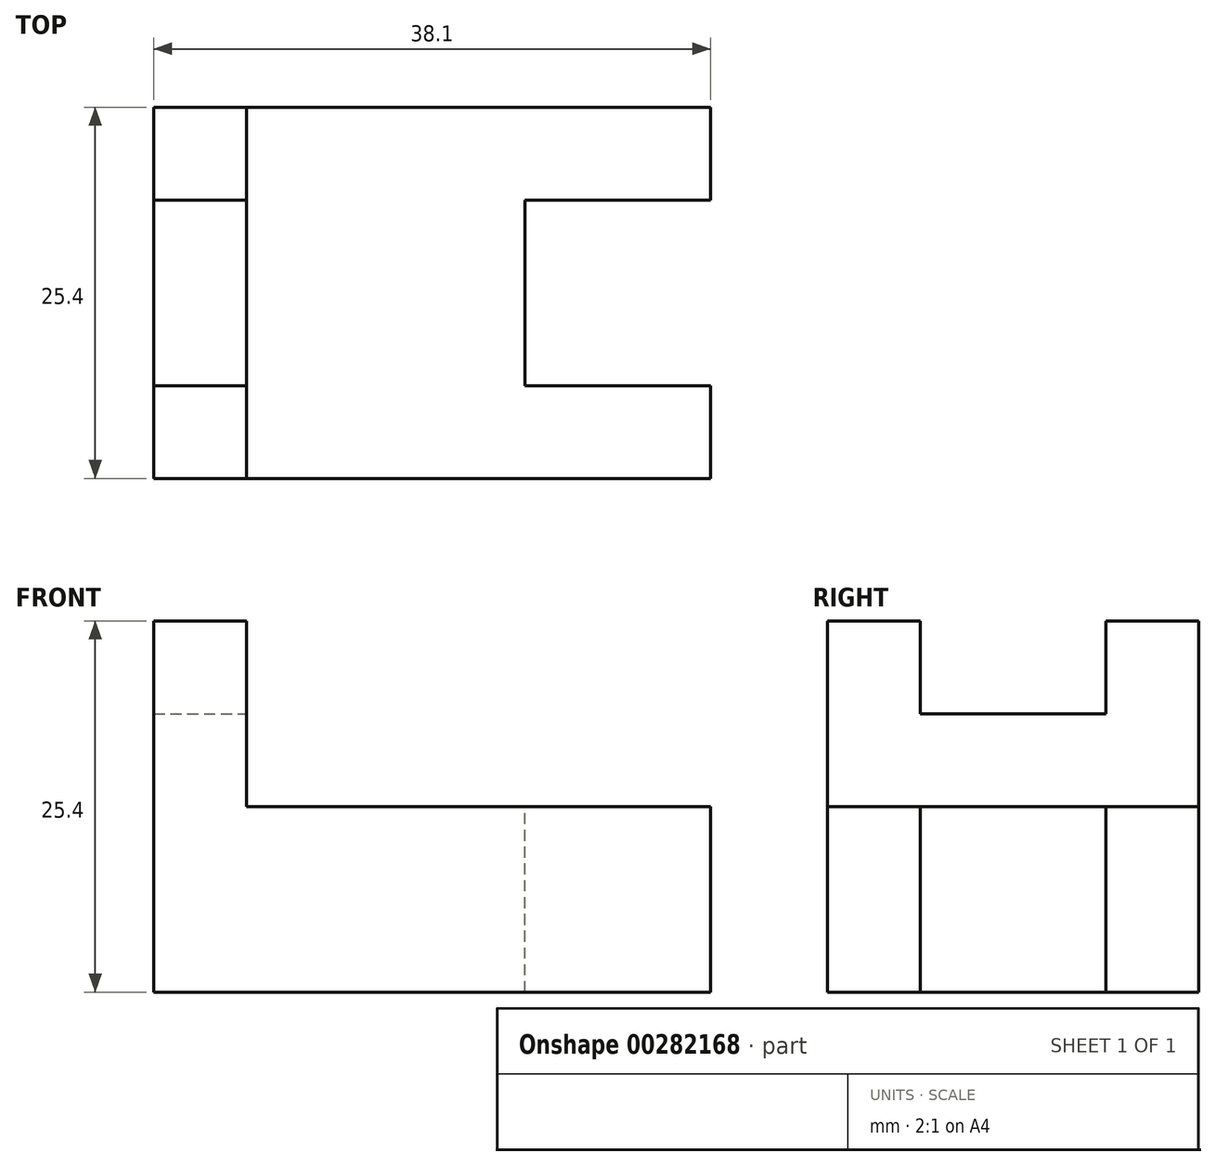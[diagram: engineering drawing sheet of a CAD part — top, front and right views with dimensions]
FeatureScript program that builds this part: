
annotation { "Feature Type Name" : "Feature", "Feature Type Description" : "" }
export const myFeature = defineFeature(function(context is Context, id is Id, definition is map)
    precondition{}
    {
        {
            var Q0;
            Q0=qCreatedBy(makeId("Front.planeOp"),FACE);
            var sketch = newSketch(context, id + "F0", { "sketchPlane" : qUnion([Q0])});
            skLineSegment(sketch, "E0", {"start": v(0, 0) * mm, "end": v(0, 25.4) * mm});
            skLineSegment(sketch, "E1", {"start": v(0, 25.4) * mm, "end": v(6.35, 25.4) * mm});
            skLineSegment(sketch, "E2", {"start": v(6.35, 25.4) * mm, "end": v(6.35, 12.7) * mm});
            skLineSegment(sketch, "E3", {"start": v(6.35, 12.7) * mm, "end": v(38.1, 12.7) * mm});
            skLineSegment(sketch, "E4", {"start": v(38.1, 12.7) * mm, "end": v(38.1, 0) * mm});
            skLineSegment(sketch, "E5", {"start": v(38.1, 0) * mm, "end": v(0, 0) * mm});
            skSolve(sketch);
        }
        {
            var Q0;
            Q0=makeQuery(id+"F0.imprint","IMPRINT",FACE,{"disambiguationData":[TD([[makeQuery(id+"F0.imprint","IMPRINT",EDGE,{"derivedFrom":sQuery(id+"F0.wireOp",EDGE,"E0")}),-1.0]])]});
            extrude(context, id + "F1", {"entities" : qUnion([Q0]), "depth" : 25.4 * mm});
        }
        {
            var Q0;
            Q0=makeQuery(id+"F1.opExtrude","SWEPT_FACE",FACE,{"disambiguationData":[OSD([sQuery(id+"F0.wireOp",EDGE,"E1")])]});
            var sketch = newSketch(context, id + "F2", { "sketchPlane" : qUnion([Q0])});
            skLineSegment(sketch, "E6.bottom", {"start": v(0, -19.05) * mm, "end": v(6.35, -19.05) * mm});
            skLineSegment(sketch, "E6.top", {"start": v(0, -6.35) * mm, "end": v(6.35, -6.35) * mm});
            skLineSegment(sketch, "E6.left", {"start": v(0, -19.05) * mm, "end": v(0, -6.35) * mm});
            skLineSegment(sketch, "E6.right", {"start": v(6.35, -19.05) * mm, "end": v(6.35, -6.35) * mm});
            skSolve(sketch);
        }
        {
            var Q0;
            Q0=makeQuery(id+"F2.imprint","IMPRINT",FACE,{"disambiguationData":[TD([[makeQuery(id+"F2.imprint","IMPRINT",EDGE,{"derivedFrom":sQuery(id+"F2.wireOp",EDGE,"E6.bottom")}),1.0]])]});
            extrude(context, id + "F3", {"entities" : qUnion([Q0]), "operationType" : NewBodyOperationType.REMOVE, "oppositeDirection" : true, "depth" : 6.35 * mm});
        }
        {
            var Q0;
            Q0=makeQuery(id+"F1.opExtrude","SWEPT_FACE",FACE,{"disambiguationData":[OSD([sQuery(id+"F0.wireOp",EDGE,"E4")])]});
            var sketch = newSketch(context, id + "F4", { "sketchPlane" : qUnion([Q0])});
            skLineSegment(sketch, "E7.bottom", {"start": v(-19.05, 0) * mm, "end": v(-6.35, 0) * mm});
            skLineSegment(sketch, "E7.top", {"start": v(-19.05, 12.7) * mm, "end": v(-6.35, 12.7) * mm});
            skLineSegment(sketch, "E7.left", {"start": v(-19.05, 0) * mm, "end": v(-19.05, 12.7) * mm});
            skLineSegment(sketch, "E7.right", {"start": v(-6.35, 0) * mm, "end": v(-6.35, 12.7) * mm});
            skSolve(sketch);
        }
        {
            var Q0;
            Q0=makeQuery(id+"F4.imprint","IMPRINT",FACE,{"disambiguationData":[TD([[makeQuery(id+"F4.imprint","IMPRINT",EDGE,{"derivedFrom":sQuery(id+"F4.wireOp",EDGE,"E7.bottom")}),1.0]])]});
            extrude(context, id + "F5", {"entities" : qUnion([Q0]), "operationType" : NewBodyOperationType.REMOVE, "oppositeDirection" : true, "depth" : 12.7 * mm});
        }
    });
